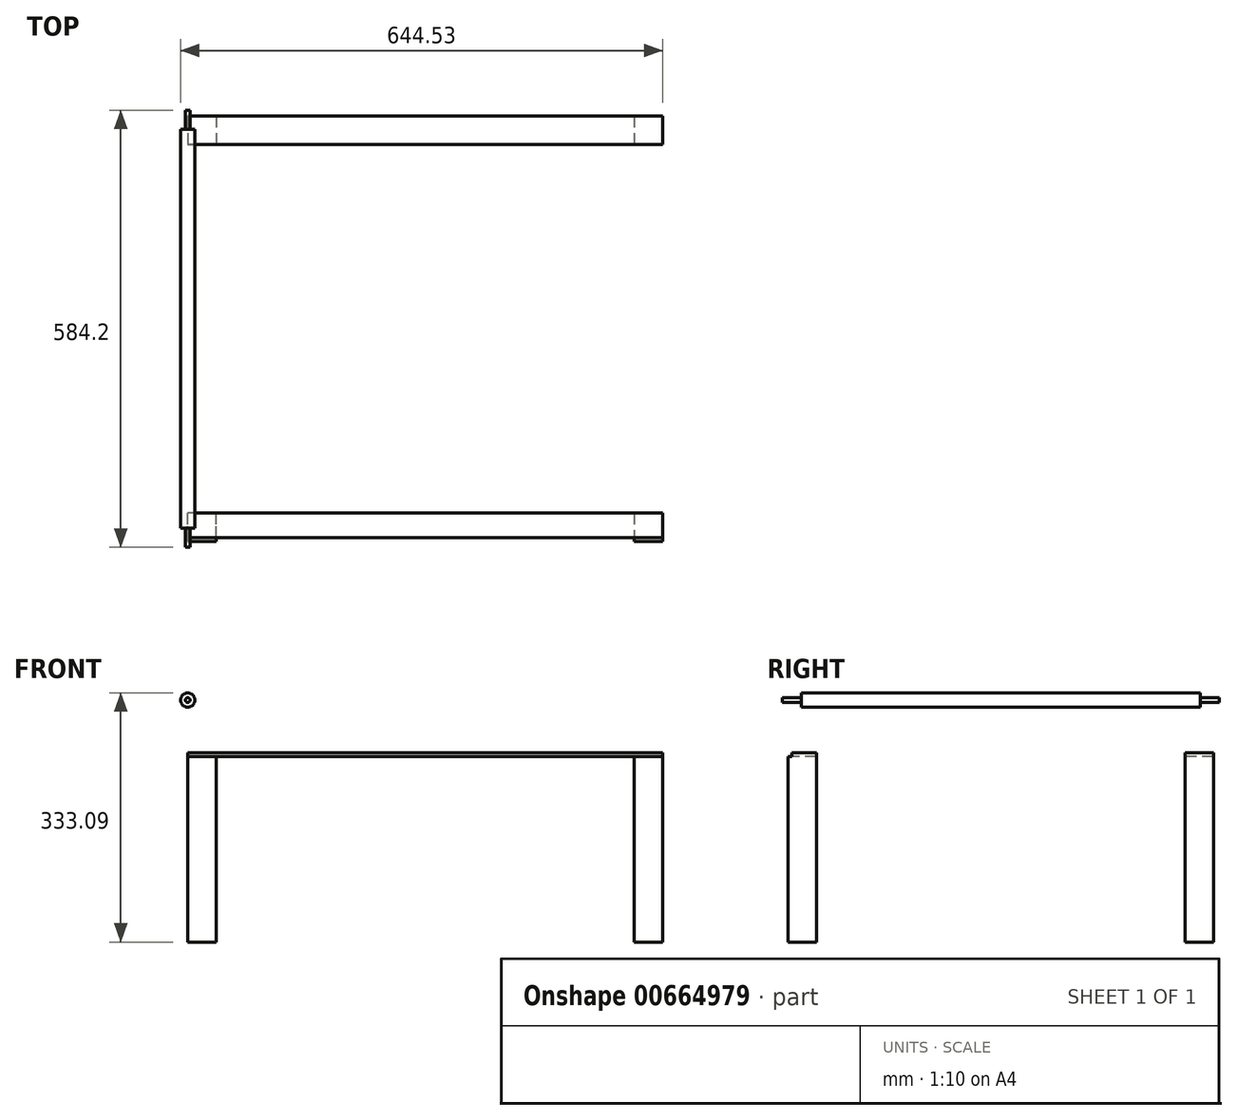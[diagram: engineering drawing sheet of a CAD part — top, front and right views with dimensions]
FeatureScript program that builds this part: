
annotation { "Feature Type Name" : "Feature", "Feature Type Description" : "" }
export const myFeature = defineFeature(function(context is Context, id is Id, definition is map)
    precondition{}
    {
        {
            var Q0;
            Q0=qCreatedBy(makeId("Front.planeOp"),FACE);
            var sketch = newSketch(context, id + "F0", { "sketchPlane" : qUnion([Q0])});
            skCircle(sketch, "E0", {"center": v(0, 0) * mm, "radius": 3.18 * mm});
            skSolve(sketch);
        }
        {
            var Q0;
            Q0=makeQuery(id+"F0.imprint","IMPRINT",FACE,{"disambiguationData":[TD([[makeQuery(id+"F0.imprint","IMPRINT",EDGE,{"derivedFrom":sQuery(id+"F0.wireOp",EDGE,"E0")}),1.0]])]});
            extrude(context, id + "F1", {"entities" : qUnion([Q0]), "endBound" : BoundingType.SYMMETRIC, "depth" : 584.2 * mm, "offsetDistance" : 25.4 * mm});
        }
        {
            var Q0;
            Q0=qCreatedBy(makeId("Front.planeOp"),FACE);
            var sketch = newSketch(context, id + "F2", { "sketchPlane" : qUnion([Q0])});
            skCircle(sketch, "E1", {"center": v(0, 0) * mm, "radius": 9.53 * mm});
            skSolve(sketch);
        }
        {
            var Q0;
            Q0=makeQuery(id+"F2.imprint","IMPRINT",FACE,{"disambiguationData":[TD([[makeQuery(id+"F2.imprint","IMPRINT",EDGE,{"derivedFrom":sQuery(id+"F2.wireOp",EDGE,"E1")}),1.0]])]});
            extrude(context, id + "F3", {"entities" : qUnion([Q0]), "operationType" : NewBodyOperationType.ADD, "endBound" : BoundingType.SYMMETRIC, "depth" : 533.4 * mm, "offsetDistance" : 25.4 * mm});
        }
        {
            var Q0;
            Q0=qCreatedBy(makeId("Right.planeOp"),FACE);
            var sketch = newSketch(context, id + "F4", { "sketchPlane" : qUnion([Q0])});
            skLineSegment(sketch, "E2.bottom", {"start": v(-284.48, -12.24) * mm, "end": v(-279.4, -12.24) * mm});
            skLineSegment(sketch, "E2.top", {"start": v(-284.48, -75.74) * mm, "end": v(-279.4, -75.74) * mm});
            skLineSegment(sketch, "E2.left", {"start": v(-284.48, -12.24) * mm, "end": v(-284.48, -75.74) * mm});
            skLineSegment(sketch, "E2.right", {"start": v(-279.4, -12.24) * mm, "end": v(-279.4, -75.74) * mm});
            skLineSegment(sketch, "E3.bottom", {"start": v(-284.48, -75.74) * mm, "end": v(-246.38, -75.74) * mm});
            skLineSegment(sketch, "E3.top", {"start": v(-284.48, -70.66) * mm, "end": v(-246.38, -70.66) * mm});
            skLineSegment(sketch, "E3.left", {"start": v(-284.48, -75.74) * mm, "end": v(-284.48, -70.66) * mm});
            skLineSegment(sketch, "E3.right", {"start": v(-246.38, -75.74) * mm, "end": v(-246.38, -70.66) * mm});
            skLineSegment(sketch, "E4", {"start": v(0, 0) * mm, "end": v(0, -41.11) * mm});
            skLineSegment(sketch, "E5.MirrorCS", {"start": v(284.48, -75.74) * mm, "end": v(284.48, -70.66) * mm});
            skLineSegment(sketch, "E6.MirrorCS", {"start": v(284.48, -12.24) * mm, "end": v(279.4, -12.24) * mm});
            skLineSegment(sketch, "E7.MirrorCS", {"start": v(246.38, -75.74) * mm, "end": v(246.38, -70.66) * mm});
            skLineSegment(sketch, "E8.MirrorCS", {"start": v(284.48, -75.74) * mm, "end": v(279.4, -75.74) * mm});
            skLineSegment(sketch, "E9.MirrorCS", {"start": v(284.48, -70.66) * mm, "end": v(246.38, -70.66) * mm});
            skLineSegment(sketch, "E10.MirrorCS", {"start": v(279.4, -12.24) * mm, "end": v(279.4, -75.74) * mm});
            skLineSegment(sketch, "E11.MirrorCS", {"start": v(284.48, -75.74) * mm, "end": v(246.38, -75.74) * mm});
            skLineSegment(sketch, "E12.MirrorCS", {"start": v(284.48, -12.24) * mm, "end": v(284.48, -75.74) * mm});
            skSolve(sketch);
        }
        {
            var Q0;
            {var subQ0=sQuery(id+"F4.wireOp",EDGE,"E2.bottom");Q0=makeQuery(id+"F4.imprint","IMPRINT",FACE,{"disambiguationData":[TD([[makeQuery(id+"F4.imprint","IMPRINT",EDGE,{"derivedFrom":subQ0}),-1.0]])]});}
            var Q1;
            {var subQ5=sQuery(id+"F4.wireOp",EDGE,"E3.left");Q1=makeQuery(id+"F4.imprint","IMPRINT",FACE,{"disambiguationData":[TD([[makeQuery(id+"F4.imprint","IMPRINT",EDGE,{"derivedFrom":subQ5}),-1.0]])]});}
            var Q2;
            {var subQ5=sQuery(id+"F4.wireOp",EDGE,"E3.right");Q2=makeQuery(id+"F4.imprint","IMPRINT",FACE,{"disambiguationData":[TD([[makeQuery(id+"F4.imprint","IMPRINT",EDGE,{"derivedFrom":subQ5}),1.0]])]});}
            var Q3;
            {var subQ0=sQuery(id+"F4.wireOp",EDGE,"E6.MirrorCS");Q3=makeQuery(id+"F4.imprint","IMPRINT",FACE,{"disambiguationData":[TD([[makeQuery(id+"F4.imprint","IMPRINT",EDGE,{"derivedFrom":subQ0}),1.0]])]});}
            var Q4;
            {var subQ0=sQuery(id+"F4.wireOp",EDGE,"E12.MirrorCS");var subQ1=sQuery(id+"F4.wireOp",EDGE,"E9.MirrorCS");var subQ2=makeQuery(id+"F4.imprint","INTERSECT",VERTEX,{"derivedFrom":[subQ1,subQ0]});Q4=makeQuery(id+"F4.imprint","IMPRINT",FACE,{"disambiguationData":[TD([[makeQuery(id+"F4.imprint","IMPRINT",EDGE,{"disambiguationData":[TD([[subQ2,-1.0]])],"derivedFrom":subQ1}),1.0]])]});}
            var Q5;
            {var subQ0=sQuery(id+"F4.wireOp",EDGE,"E7.MirrorCS");Q5=makeQuery(id+"F4.imprint","IMPRINT",FACE,{"disambiguationData":[TD([[makeQuery(id+"F4.imprint","IMPRINT",EDGE,{"derivedFrom":subQ0}),-1.0]])]});}
            extrude(context, id + "F5", {"entities" : qUnion([Q0, Q1, Q2, Q3, Q4, Q5]), "depth" : 635 * mm, "offsetDistance" : 25.4 * mm});
        }
        {
            var Q0;
            Q0=makeQuery(id+"F5.opExtrude","SWEPT_FACE",FACE,{"disambiguationData":[OSD([sQuery(id+"F4.wireOp",EDGE,"E2.left"),sQuery(id+"F4.wireOp",EDGE,"E3.left")])]});
            var sketch = newSketch(context, id + "F6", { "sketchPlane" : qUnion([Q0])});
            skLineSegment(sketch, "E13", {"start": v(0, -40.81) * mm, "end": v(635, -40.81) * mm});
            skCircle(sketch, "E14", {"center": v(9.53, -40.81) * mm, "radius": 3.18 * mm});
            skCircle(sketch, "E15.1.0.0", {"center": v(53.98, -40.81) * mm, "radius": 3.18 * mm});
            skCircle(sketch, "E15.2.0.0", {"center": v(98.43, -40.81) * mm, "radius": 3.18 * mm});
            skCircle(sketch, "E15.3.0.0", {"center": v(142.88, -40.81) * mm, "radius": 3.18 * mm});
            skCircle(sketch, "E15.4.0.0", {"center": v(187.33, -40.81) * mm, "radius": 3.18 * mm});
            skCircle(sketch, "E15.5.0.0", {"center": v(231.78, -40.81) * mm, "radius": 3.18 * mm});
            skCircle(sketch, "E15.6.0.0", {"center": v(276.23, -40.81) * mm, "radius": 3.18 * mm});
            skCircle(sketch, "E15.7.0.0", {"center": v(320.68, -40.81) * mm, "radius": 3.18 * mm});
            skLineSegment(sketch, "E15.direction1", {"start": v(9.53, -40.81) * mm, "end": v(53.98, -40.81) * mm, "construction": true});
            skLineSegment(sketch, "E16", {"start": v(0, -18.59) * mm, "end": v(393.7, -18.59) * mm});
            skCircle(sketch, "E17", {"center": v(9.53, -18.59) * mm, "radius": 3.18 * mm});
            skCircle(sketch, "E18.1.0.0", {"center": v(53.98, -18.59) * mm, "radius": 3.18 * mm});
            skCircle(sketch, "E18.2.0.0", {"center": v(98.43, -18.59) * mm, "radius": 3.18 * mm});
            skCircle(sketch, "E18.3.0.0", {"center": v(142.88, -18.59) * mm, "radius": 3.18 * mm});
            skCircle(sketch, "E18.4.0.0", {"center": v(187.33, -18.59) * mm, "radius": 3.18 * mm});
            skCircle(sketch, "E18.5.0.0", {"center": v(231.78, -18.59) * mm, "radius": 3.18 * mm});
            skCircle(sketch, "E18.6.0.0", {"center": v(276.23, -18.59) * mm, "radius": 3.18 * mm});
            skCircle(sketch, "E18.7.0.0", {"center": v(320.68, -18.59) * mm, "radius": 3.18 * mm});
            skLineSegment(sketch, "E18.direction1", {"start": v(9.53, -18.59) * mm, "end": v(53.98, -18.59) * mm, "construction": true});
            skCircle(sketch, "E19.0.8.0", {"center": v(365.13, -18.59) * mm, "radius": 3.18 * mm});
            skCircle(sketch, "E20.0.8.0", {"center": v(365.13, -40.81) * mm, "radius": 3.18 * mm});
            skCircle(sketch, "E21.0.9.0", {"center": v(409.58, -40.81) * mm, "radius": 3.18 * mm});
            skCircle(sketch, "E21.0.10.0", {"center": v(454.03, -40.81) * mm, "radius": 3.18 * mm});
            skCircle(sketch, "E21.0.11.0", {"center": v(498.48, -40.81) * mm, "radius": 3.18 * mm});
            skCircle(sketch, "E21.0.12.0", {"center": v(542.93, -40.81) * mm, "radius": 3.18 * mm});
            skCircle(sketch, "E21.0.13.0", {"center": v(587.38, -40.81) * mm, "radius": 3.18 * mm});
            skCircle(sketch, "E22.0.9.0", {"center": v(409.58, -18.59) * mm, "radius": 3.18 * mm});
            skCircle(sketch, "E22.0.10.0", {"center": v(454.03, -18.59) * mm, "radius": 3.18 * mm});
            skCircle(sketch, "E22.0.11.0", {"center": v(498.48, -18.59) * mm, "radius": 3.18 * mm});
            skCircle(sketch, "E22.0.12.0", {"center": v(542.93, -18.59) * mm, "radius": 3.18 * mm});
            skCircle(sketch, "E22.0.13.0", {"center": v(587.38, -18.59) * mm, "radius": 3.18 * mm});
            skLineSegment(sketch, "E23", {"start": v(393.7, -18.59) * mm, "end": v(635, -18.59) * mm});
            skSolve(sketch);
        }
        {
            var Q0;
            {var subQ0=sQuery(id+"F6.wireOp",EDGE,"E14");var subQ1=sQuery(id+"F6.wireOp",EDGE,"E13");var subQ2=makeQuery(id+"F6.imprint","INTERSECT",VERTEX,{"disambiguationData":[OD(0.0)],"derivedFrom":[subQ1,subQ0]});Q0=makeQuery(id+"F6.imprint","IMPRINT",FACE,{"disambiguationData":[TD([[makeQuery(id+"F6.imprint","IMPRINT",EDGE,{"disambiguationData":[TD([[subQ2,-1.0]])],"derivedFrom":subQ1}),1.0]])]});}
            var Q1;
            {var subQ0=sQuery(id+"F6.wireOp",EDGE,"E14");var subQ1=sQuery(id+"F6.wireOp",EDGE,"E13");var subQ2=makeQuery(id+"F6.imprint","INTERSECT",VERTEX,{"disambiguationData":[OD(0.0)],"derivedFrom":[subQ1,subQ0]});Q1=makeQuery(id+"F6.imprint","IMPRINT",FACE,{"disambiguationData":[TD([[makeQuery(id+"F6.imprint","IMPRINT",EDGE,{"disambiguationData":[TD([[subQ2,-1.0]])],"derivedFrom":subQ1}),-1.0]])]});}
            var Q2;
            {var subQ0=sQuery(id+"F6.wireOp",EDGE,"E15.1.0.0");var subQ1=sQuery(id+"F6.wireOp",EDGE,"E13");var subQ2=makeQuery(id+"F6.imprint","INTERSECT",VERTEX,{"disambiguationData":[OD(0.0)],"derivedFrom":[subQ1,subQ0]});Q2=makeQuery(id+"F6.imprint","IMPRINT",FACE,{"disambiguationData":[TD([[makeQuery(id+"F6.imprint","IMPRINT",EDGE,{"disambiguationData":[TD([[subQ2,-1.0]])],"derivedFrom":subQ1}),1.0]])]});}
            var Q3;
            {var subQ0=sQuery(id+"F6.wireOp",EDGE,"E15.2.0.0");var subQ1=sQuery(id+"F6.wireOp",EDGE,"E13");var subQ2=makeQuery(id+"F6.imprint","INTERSECT",VERTEX,{"disambiguationData":[OD(0.0)],"derivedFrom":[subQ1,subQ0]});Q3=makeQuery(id+"F6.imprint","IMPRINT",FACE,{"disambiguationData":[TD([[makeQuery(id+"F6.imprint","IMPRINT",EDGE,{"disambiguationData":[TD([[subQ2,-1.0]])],"derivedFrom":subQ1}),1.0]])]});}
            var Q4;
            {var subQ0=sQuery(id+"F6.wireOp",EDGE,"E15.2.0.0");var subQ1=sQuery(id+"F6.wireOp",EDGE,"E13");var subQ2=makeQuery(id+"F6.imprint","INTERSECT",VERTEX,{"disambiguationData":[OD(0.0)],"derivedFrom":[subQ1,subQ0]});Q4=makeQuery(id+"F6.imprint","IMPRINT",FACE,{"disambiguationData":[TD([[makeQuery(id+"F6.imprint","IMPRINT",EDGE,{"disambiguationData":[TD([[subQ2,-1.0]])],"derivedFrom":subQ1}),-1.0]])]});}
            var Q5;
            {var subQ0=sQuery(id+"F6.wireOp",EDGE,"E15.1.0.0");var subQ1=sQuery(id+"F6.wireOp",EDGE,"E13");var subQ2=makeQuery(id+"F6.imprint","INTERSECT",VERTEX,{"disambiguationData":[OD(0.0)],"derivedFrom":[subQ1,subQ0]});Q5=makeQuery(id+"F6.imprint","IMPRINT",FACE,{"disambiguationData":[TD([[makeQuery(id+"F6.imprint","IMPRINT",EDGE,{"disambiguationData":[TD([[subQ2,-1.0]])],"derivedFrom":subQ1}),-1.0]])]});}
            var Q6;
            {var subQ0=sQuery(id+"F6.wireOp",EDGE,"E15.3.0.0");var subQ1=sQuery(id+"F6.wireOp",EDGE,"E13");var subQ2=makeQuery(id+"F6.imprint","INTERSECT",VERTEX,{"disambiguationData":[OD(0.0)],"derivedFrom":[subQ1,subQ0]});Q6=makeQuery(id+"F6.imprint","IMPRINT",FACE,{"disambiguationData":[TD([[makeQuery(id+"F6.imprint","IMPRINT",EDGE,{"disambiguationData":[TD([[subQ2,-1.0]])],"derivedFrom":subQ1}),-1.0]])]});}
            var Q7;
            {var subQ0=sQuery(id+"F6.wireOp",EDGE,"E15.3.0.0");var subQ1=sQuery(id+"F6.wireOp",EDGE,"E13");var subQ2=makeQuery(id+"F6.imprint","INTERSECT",VERTEX,{"disambiguationData":[OD(0.0)],"derivedFrom":[subQ1,subQ0]});Q7=makeQuery(id+"F6.imprint","IMPRINT",FACE,{"disambiguationData":[TD([[makeQuery(id+"F6.imprint","IMPRINT",EDGE,{"disambiguationData":[TD([[subQ2,-1.0]])],"derivedFrom":subQ1}),1.0]])]});}
            var Q8;
            {var subQ0=sQuery(id+"F6.wireOp",EDGE,"E15.4.0.0");var subQ1=sQuery(id+"F6.wireOp",EDGE,"E13");var subQ2=makeQuery(id+"F6.imprint","INTERSECT",VERTEX,{"disambiguationData":[OD(0.0)],"derivedFrom":[subQ1,subQ0]});Q8=makeQuery(id+"F6.imprint","IMPRINT",FACE,{"disambiguationData":[TD([[makeQuery(id+"F6.imprint","IMPRINT",EDGE,{"disambiguationData":[TD([[subQ2,-1.0]])],"derivedFrom":subQ1}),1.0]])]});}
            var Q9;
            {var subQ0=sQuery(id+"F6.wireOp",EDGE,"E15.4.0.0");var subQ1=sQuery(id+"F6.wireOp",EDGE,"E13");var subQ2=makeQuery(id+"F6.imprint","INTERSECT",VERTEX,{"disambiguationData":[OD(0.0)],"derivedFrom":[subQ1,subQ0]});Q9=makeQuery(id+"F6.imprint","IMPRINT",FACE,{"disambiguationData":[TD([[makeQuery(id+"F6.imprint","IMPRINT",EDGE,{"disambiguationData":[TD([[subQ2,-1.0]])],"derivedFrom":subQ1}),-1.0]])]});}
            var Q10;
            {var subQ0=sQuery(id+"F6.wireOp",EDGE,"E15.5.0.0");var subQ1=sQuery(id+"F6.wireOp",EDGE,"E13");var subQ2=makeQuery(id+"F6.imprint","INTERSECT",VERTEX,{"disambiguationData":[OD(0.0)],"derivedFrom":[subQ1,subQ0]});Q10=makeQuery(id+"F6.imprint","IMPRINT",FACE,{"disambiguationData":[TD([[makeQuery(id+"F6.imprint","IMPRINT",EDGE,{"disambiguationData":[TD([[subQ2,-1.0]])],"derivedFrom":subQ1}),1.0]])]});}
            var Q11;
            {var subQ0=sQuery(id+"F6.wireOp",EDGE,"E15.5.0.0");var subQ1=sQuery(id+"F6.wireOp",EDGE,"E13");var subQ2=makeQuery(id+"F6.imprint","INTERSECT",VERTEX,{"disambiguationData":[OD(0.0)],"derivedFrom":[subQ1,subQ0]});Q11=makeQuery(id+"F6.imprint","IMPRINT",FACE,{"disambiguationData":[TD([[makeQuery(id+"F6.imprint","IMPRINT",EDGE,{"disambiguationData":[TD([[subQ2,-1.0]])],"derivedFrom":subQ1}),-1.0]])]});}
            var Q12;
            {var subQ0=sQuery(id+"F6.wireOp",EDGE,"E15.6.0.0");var subQ1=sQuery(id+"F6.wireOp",EDGE,"E13");var subQ2=makeQuery(id+"F6.imprint","INTERSECT",VERTEX,{"disambiguationData":[OD(0.0)],"derivedFrom":[subQ1,subQ0]});Q12=makeQuery(id+"F6.imprint","IMPRINT",FACE,{"disambiguationData":[TD([[makeQuery(id+"F6.imprint","IMPRINT",EDGE,{"disambiguationData":[TD([[subQ2,-1.0]])],"derivedFrom":subQ1}),-1.0]])]});}
            var Q13;
            {var subQ0=sQuery(id+"F6.wireOp",EDGE,"E15.6.0.0");var subQ1=sQuery(id+"F6.wireOp",EDGE,"E13");var subQ2=makeQuery(id+"F6.imprint","INTERSECT",VERTEX,{"disambiguationData":[OD(0.0)],"derivedFrom":[subQ1,subQ0]});Q13=makeQuery(id+"F6.imprint","IMPRINT",FACE,{"disambiguationData":[TD([[makeQuery(id+"F6.imprint","IMPRINT",EDGE,{"disambiguationData":[TD([[subQ2,-1.0]])],"derivedFrom":subQ1}),1.0]])]});}
            var Q14;
            {var subQ0=sQuery(id+"F6.wireOp",EDGE,"E15.7.0.0");var subQ1=sQuery(id+"F6.wireOp",EDGE,"E13");var subQ2=makeQuery(id+"F6.imprint","INTERSECT",VERTEX,{"disambiguationData":[OD(0.0)],"derivedFrom":[subQ1,subQ0]});Q14=makeQuery(id+"F6.imprint","IMPRINT",FACE,{"disambiguationData":[TD([[makeQuery(id+"F6.imprint","IMPRINT",EDGE,{"disambiguationData":[TD([[subQ2,-1.0]])],"derivedFrom":subQ1}),-1.0]])]});}
            var Q15;
            {var subQ0=sQuery(id+"F6.wireOp",EDGE,"E15.7.0.0");var subQ1=sQuery(id+"F6.wireOp",EDGE,"E13");var subQ2=makeQuery(id+"F6.imprint","INTERSECT",VERTEX,{"disambiguationData":[OD(0.0)],"derivedFrom":[subQ1,subQ0]});Q15=makeQuery(id+"F6.imprint","IMPRINT",FACE,{"disambiguationData":[TD([[makeQuery(id+"F6.imprint","IMPRINT",EDGE,{"disambiguationData":[TD([[subQ2,-1.0]])],"derivedFrom":subQ1}),1.0]])]});}
            var Q16;
            {var subQ0=sQuery(id+"F6.wireOp",EDGE,"E17");var subQ1=sQuery(id+"F6.wireOp",EDGE,"E16");var subQ2=makeQuery(id+"F6.imprint","INTERSECT",VERTEX,{"disambiguationData":[OD(0.0)],"derivedFrom":[subQ1,subQ0]});Q16=makeQuery(id+"F6.imprint","IMPRINT",FACE,{"disambiguationData":[TD([[makeQuery(id+"F6.imprint","IMPRINT",EDGE,{"disambiguationData":[TD([[subQ2,-1.0]])],"derivedFrom":subQ1}),1.0]])]});}
            var Q17;
            {var subQ0=sQuery(id+"F6.wireOp",EDGE,"E17");var subQ1=sQuery(id+"F6.wireOp",EDGE,"E16");var subQ2=makeQuery(id+"F6.imprint","INTERSECT",VERTEX,{"disambiguationData":[OD(0.0)],"derivedFrom":[subQ1,subQ0]});Q17=makeQuery(id+"F6.imprint","IMPRINT",FACE,{"disambiguationData":[TD([[makeQuery(id+"F6.imprint","IMPRINT",EDGE,{"disambiguationData":[TD([[subQ2,-1.0]])],"derivedFrom":subQ1}),-1.0]])]});}
            var Q18;
            {var subQ0=sQuery(id+"F6.wireOp",EDGE,"E18.1.0.0");var subQ1=sQuery(id+"F6.wireOp",EDGE,"E16");var subQ2=makeQuery(id+"F6.imprint","INTERSECT",VERTEX,{"disambiguationData":[OD(0.0)],"derivedFrom":[subQ1,subQ0]});Q18=makeQuery(id+"F6.imprint","IMPRINT",FACE,{"disambiguationData":[TD([[makeQuery(id+"F6.imprint","IMPRINT",EDGE,{"disambiguationData":[TD([[subQ2,-1.0]])],"derivedFrom":subQ1}),1.0]])]});}
            var Q19;
            {var subQ0=sQuery(id+"F6.wireOp",EDGE,"E18.1.0.0");var subQ1=sQuery(id+"F6.wireOp",EDGE,"E16");var subQ2=makeQuery(id+"F6.imprint","INTERSECT",VERTEX,{"disambiguationData":[OD(0.0)],"derivedFrom":[subQ1,subQ0]});Q19=makeQuery(id+"F6.imprint","IMPRINT",FACE,{"disambiguationData":[TD([[makeQuery(id+"F6.imprint","IMPRINT",EDGE,{"disambiguationData":[TD([[subQ2,-1.0]])],"derivedFrom":subQ1}),-1.0]])]});}
            var Q20;
            {var subQ0=sQuery(id+"F6.wireOp",EDGE,"E18.2.0.0");var subQ1=sQuery(id+"F6.wireOp",EDGE,"E16");var subQ2=makeQuery(id+"F6.imprint","INTERSECT",VERTEX,{"disambiguationData":[OD(0.0)],"derivedFrom":[subQ1,subQ0]});Q20=makeQuery(id+"F6.imprint","IMPRINT",FACE,{"disambiguationData":[TD([[makeQuery(id+"F6.imprint","IMPRINT",EDGE,{"disambiguationData":[TD([[subQ2,-1.0]])],"derivedFrom":subQ1}),-1.0]])]});}
            var Q21;
            {var subQ0=sQuery(id+"F6.wireOp",EDGE,"E18.2.0.0");var subQ1=sQuery(id+"F6.wireOp",EDGE,"E16");var subQ2=makeQuery(id+"F6.imprint","INTERSECT",VERTEX,{"disambiguationData":[OD(0.0)],"derivedFrom":[subQ1,subQ0]});Q21=makeQuery(id+"F6.imprint","IMPRINT",FACE,{"disambiguationData":[TD([[makeQuery(id+"F6.imprint","IMPRINT",EDGE,{"disambiguationData":[TD([[subQ2,-1.0]])],"derivedFrom":subQ1}),1.0]])]});}
            var Q22;
            {var subQ0=sQuery(id+"F6.wireOp",EDGE,"E18.3.0.0");var subQ1=sQuery(id+"F6.wireOp",EDGE,"E16");var subQ2=makeQuery(id+"F6.imprint","INTERSECT",VERTEX,{"disambiguationData":[OD(0.0)],"derivedFrom":[subQ1,subQ0]});Q22=makeQuery(id+"F6.imprint","IMPRINT",FACE,{"disambiguationData":[TD([[makeQuery(id+"F6.imprint","IMPRINT",EDGE,{"disambiguationData":[TD([[subQ2,-1.0]])],"derivedFrom":subQ1}),-1.0]])]});}
            var Q23;
            {var subQ0=sQuery(id+"F6.wireOp",EDGE,"E18.3.0.0");var subQ1=sQuery(id+"F6.wireOp",EDGE,"E16");var subQ2=makeQuery(id+"F6.imprint","INTERSECT",VERTEX,{"disambiguationData":[OD(0.0)],"derivedFrom":[subQ1,subQ0]});Q23=makeQuery(id+"F6.imprint","IMPRINT",FACE,{"disambiguationData":[TD([[makeQuery(id+"F6.imprint","IMPRINT",EDGE,{"disambiguationData":[TD([[subQ2,-1.0]])],"derivedFrom":subQ1}),1.0]])]});}
            var Q24;
            {var subQ0=sQuery(id+"F6.wireOp",EDGE,"E18.4.0.0");var subQ1=sQuery(id+"F6.wireOp",EDGE,"E16");var subQ2=makeQuery(id+"F6.imprint","INTERSECT",VERTEX,{"disambiguationData":[OD(0.0)],"derivedFrom":[subQ1,subQ0]});Q24=makeQuery(id+"F6.imprint","IMPRINT",FACE,{"disambiguationData":[TD([[makeQuery(id+"F6.imprint","IMPRINT",EDGE,{"disambiguationData":[TD([[subQ2,-1.0]])],"derivedFrom":subQ1}),-1.0]])]});}
            var Q25;
            {var subQ0=sQuery(id+"F6.wireOp",EDGE,"E18.4.0.0");var subQ1=sQuery(id+"F6.wireOp",EDGE,"E16");var subQ2=makeQuery(id+"F6.imprint","INTERSECT",VERTEX,{"disambiguationData":[OD(0.0)],"derivedFrom":[subQ1,subQ0]});Q25=makeQuery(id+"F6.imprint","IMPRINT",FACE,{"disambiguationData":[TD([[makeQuery(id+"F6.imprint","IMPRINT",EDGE,{"disambiguationData":[TD([[subQ2,-1.0]])],"derivedFrom":subQ1}),1.0]])]});}
            var Q26;
            {var subQ0=sQuery(id+"F6.wireOp",EDGE,"E18.5.0.0");var subQ1=sQuery(id+"F6.wireOp",EDGE,"E16");var subQ2=makeQuery(id+"F6.imprint","INTERSECT",VERTEX,{"disambiguationData":[OD(0.0)],"derivedFrom":[subQ1,subQ0]});Q26=makeQuery(id+"F6.imprint","IMPRINT",FACE,{"disambiguationData":[TD([[makeQuery(id+"F6.imprint","IMPRINT",EDGE,{"disambiguationData":[TD([[subQ2,-1.0]])],"derivedFrom":subQ1}),-1.0]])]});}
            var Q27;
            {var subQ0=sQuery(id+"F6.wireOp",EDGE,"E18.5.0.0");var subQ1=sQuery(id+"F6.wireOp",EDGE,"E16");var subQ2=makeQuery(id+"F6.imprint","INTERSECT",VERTEX,{"disambiguationData":[OD(0.0)],"derivedFrom":[subQ1,subQ0]});Q27=makeQuery(id+"F6.imprint","IMPRINT",FACE,{"disambiguationData":[TD([[makeQuery(id+"F6.imprint","IMPRINT",EDGE,{"disambiguationData":[TD([[subQ2,-1.0]])],"derivedFrom":subQ1}),1.0]])]});}
            var Q28;
            {var subQ0=sQuery(id+"F6.wireOp",EDGE,"E18.6.0.0");var subQ1=sQuery(id+"F6.wireOp",EDGE,"E16");var subQ2=makeQuery(id+"F6.imprint","INTERSECT",VERTEX,{"disambiguationData":[OD(0.0)],"derivedFrom":[subQ1,subQ0]});Q28=makeQuery(id+"F6.imprint","IMPRINT",FACE,{"disambiguationData":[TD([[makeQuery(id+"F6.imprint","IMPRINT",EDGE,{"disambiguationData":[TD([[subQ2,-1.0]])],"derivedFrom":subQ1}),-1.0]])]});}
            var Q29;
            {var subQ0=sQuery(id+"F6.wireOp",EDGE,"E18.6.0.0");var subQ1=sQuery(id+"F6.wireOp",EDGE,"E16");var subQ2=makeQuery(id+"F6.imprint","INTERSECT",VERTEX,{"disambiguationData":[OD(0.0)],"derivedFrom":[subQ1,subQ0]});Q29=makeQuery(id+"F6.imprint","IMPRINT",FACE,{"disambiguationData":[TD([[makeQuery(id+"F6.imprint","IMPRINT",EDGE,{"disambiguationData":[TD([[subQ2,-1.0]])],"derivedFrom":subQ1}),1.0]])]});}
            var Q30;
            {var subQ0=sQuery(id+"F6.wireOp",EDGE,"E18.7.0.0");var subQ1=sQuery(id+"F6.wireOp",EDGE,"E16");var subQ2=makeQuery(id+"F6.imprint","INTERSECT",VERTEX,{"disambiguationData":[OD(0.0)],"derivedFrom":[subQ1,subQ0]});Q30=makeQuery(id+"F6.imprint","IMPRINT",FACE,{"disambiguationData":[TD([[makeQuery(id+"F6.imprint","IMPRINT",EDGE,{"disambiguationData":[TD([[subQ2,-1.0]])],"derivedFrom":subQ1}),-1.0]])]});}
            var Q31;
            {var subQ0=sQuery(id+"F6.wireOp",EDGE,"E18.7.0.0");var subQ1=sQuery(id+"F6.wireOp",EDGE,"E16");var subQ2=makeQuery(id+"F6.imprint","INTERSECT",VERTEX,{"disambiguationData":[OD(0.0)],"derivedFrom":[subQ1,subQ0]});Q31=makeQuery(id+"F6.imprint","IMPRINT",FACE,{"disambiguationData":[TD([[makeQuery(id+"F6.imprint","IMPRINT",EDGE,{"disambiguationData":[TD([[subQ2,-1.0]])],"derivedFrom":subQ1}),1.0]])]});}
            var Q32;
            {var subQ0=sQuery(id+"F6.wireOp",EDGE,"E20.0.8.0");var subQ1=sQuery(id+"F6.wireOp",EDGE,"E13");var subQ2=makeQuery(id+"F6.imprint","INTERSECT",VERTEX,{"disambiguationData":[OD(0.0)],"derivedFrom":[subQ1,subQ0]});Q32=makeQuery(id+"F6.imprint","IMPRINT",FACE,{"disambiguationData":[TD([[makeQuery(id+"F6.imprint","IMPRINT",EDGE,{"disambiguationData":[TD([[subQ2,-1.0]])],"derivedFrom":subQ1}),-1.0]])]});}
            var Q33;
            {var subQ0=sQuery(id+"F6.wireOp",EDGE,"E20.0.8.0");var subQ1=sQuery(id+"F6.wireOp",EDGE,"E13");var subQ2=makeQuery(id+"F6.imprint","INTERSECT",VERTEX,{"disambiguationData":[OD(0.0)],"derivedFrom":[subQ1,subQ0]});Q33=makeQuery(id+"F6.imprint","IMPRINT",FACE,{"disambiguationData":[TD([[makeQuery(id+"F6.imprint","IMPRINT",EDGE,{"disambiguationData":[TD([[subQ2,-1.0]])],"derivedFrom":subQ1}),1.0]])]});}
            var Q34;
            {var subQ0=sQuery(id+"F6.wireOp",EDGE,"E19.0.8.0");var subQ1=sQuery(id+"F6.wireOp",EDGE,"E16");var subQ2=makeQuery(id+"F6.imprint","INTERSECT",VERTEX,{"disambiguationData":[OD(0.0)],"derivedFrom":[subQ1,subQ0]});Q34=makeQuery(id+"F6.imprint","IMPRINT",FACE,{"disambiguationData":[TD([[makeQuery(id+"F6.imprint","IMPRINT",EDGE,{"disambiguationData":[TD([[subQ2,-1.0]])],"derivedFrom":subQ1}),1.0]])]});}
            var Q35;
            {var subQ0=sQuery(id+"F6.wireOp",EDGE,"E19.0.8.0");var subQ1=sQuery(id+"F6.wireOp",EDGE,"E16");var subQ2=makeQuery(id+"F6.imprint","INTERSECT",VERTEX,{"disambiguationData":[OD(0.0)],"derivedFrom":[subQ1,subQ0]});Q35=makeQuery(id+"F6.imprint","IMPRINT",FACE,{"disambiguationData":[TD([[makeQuery(id+"F6.imprint","IMPRINT",EDGE,{"disambiguationData":[TD([[subQ2,-1.0]])],"derivedFrom":subQ1}),-1.0]])]});}
            var Q36;
            {var subQ0=sQuery(id+"F6.wireOp",EDGE,"E23");var subQ1=sQuery(id+"F6.wireOp",EDGE,"E22.0.9.0");var subQ2=makeQuery(id+"F6.imprint","INTERSECT",VERTEX,{"disambiguationData":[OD(0.0)],"derivedFrom":[subQ1,subQ0]});Q36=makeQuery(id+"F6.imprint","IMPRINT",FACE,{"disambiguationData":[TD([[makeQuery(id+"F6.imprint","IMPRINT",EDGE,{"disambiguationData":[TD([[subQ2,-1.0]])],"derivedFrom":subQ1}),1.0]])]});}
            var Q37;
            {var subQ0=sQuery(id+"F6.wireOp",EDGE,"E23");var subQ1=sQuery(id+"F6.wireOp",EDGE,"E22.0.9.0");var subQ2=makeQuery(id+"F6.imprint","INTERSECT",VERTEX,{"disambiguationData":[OD(0.0)],"derivedFrom":[subQ1,subQ0]});Q37=makeQuery(id+"F6.imprint","IMPRINT",FACE,{"disambiguationData":[TD([[makeQuery(id+"F6.imprint","IMPRINT",EDGE,{"disambiguationData":[TD([[subQ2,1.0]])],"derivedFrom":subQ1}),1.0]])]});}
            var Q38;
            {var subQ0=sQuery(id+"F6.wireOp",EDGE,"E23");var subQ1=sQuery(id+"F6.wireOp",EDGE,"E22.0.10.0");var subQ2=makeQuery(id+"F6.imprint","INTERSECT",VERTEX,{"disambiguationData":[OD(0.0)],"derivedFrom":[subQ1,subQ0]});Q38=makeQuery(id+"F6.imprint","IMPRINT",FACE,{"disambiguationData":[TD([[makeQuery(id+"F6.imprint","IMPRINT",EDGE,{"disambiguationData":[TD([[subQ2,1.0]])],"derivedFrom":subQ1}),1.0]])]});}
            var Q39;
            {var subQ0=sQuery(id+"F6.wireOp",EDGE,"E23");var subQ1=sQuery(id+"F6.wireOp",EDGE,"E22.0.10.0");var subQ2=makeQuery(id+"F6.imprint","INTERSECT",VERTEX,{"disambiguationData":[OD(0.0)],"derivedFrom":[subQ1,subQ0]});Q39=makeQuery(id+"F6.imprint","IMPRINT",FACE,{"disambiguationData":[TD([[makeQuery(id+"F6.imprint","IMPRINT",EDGE,{"disambiguationData":[TD([[subQ2,-1.0]])],"derivedFrom":subQ1}),1.0]])]});}
            var Q40;
            {var subQ0=sQuery(id+"F6.wireOp",EDGE,"E23");var subQ1=sQuery(id+"F6.wireOp",EDGE,"E22.0.11.0");var subQ2=makeQuery(id+"F6.imprint","INTERSECT",VERTEX,{"disambiguationData":[OD(0.0)],"derivedFrom":[subQ1,subQ0]});Q40=makeQuery(id+"F6.imprint","IMPRINT",FACE,{"disambiguationData":[TD([[makeQuery(id+"F6.imprint","IMPRINT",EDGE,{"disambiguationData":[TD([[subQ2,1.0]])],"derivedFrom":subQ1}),1.0]])]});}
            var Q41;
            {var subQ0=sQuery(id+"F6.wireOp",EDGE,"E23");var subQ1=sQuery(id+"F6.wireOp",EDGE,"E22.0.11.0");var subQ2=makeQuery(id+"F6.imprint","INTERSECT",VERTEX,{"disambiguationData":[OD(0.0)],"derivedFrom":[subQ1,subQ0]});Q41=makeQuery(id+"F6.imprint","IMPRINT",FACE,{"disambiguationData":[TD([[makeQuery(id+"F6.imprint","IMPRINT",EDGE,{"disambiguationData":[TD([[subQ2,-1.0]])],"derivedFrom":subQ1}),1.0]])]});}
            var Q42;
            {var subQ0=sQuery(id+"F6.wireOp",EDGE,"E23");var subQ1=sQuery(id+"F6.wireOp",EDGE,"E22.0.12.0");var subQ2=makeQuery(id+"F6.imprint","INTERSECT",VERTEX,{"disambiguationData":[OD(0.0)],"derivedFrom":[subQ1,subQ0]});Q42=makeQuery(id+"F6.imprint","IMPRINT",FACE,{"disambiguationData":[TD([[makeQuery(id+"F6.imprint","IMPRINT",EDGE,{"disambiguationData":[TD([[subQ2,1.0]])],"derivedFrom":subQ1}),1.0]])]});}
            var Q43;
            {var subQ0=sQuery(id+"F6.wireOp",EDGE,"E23");var subQ1=sQuery(id+"F6.wireOp",EDGE,"E22.0.12.0");var subQ2=makeQuery(id+"F6.imprint","INTERSECT",VERTEX,{"disambiguationData":[OD(0.0)],"derivedFrom":[subQ1,subQ0]});Q43=makeQuery(id+"F6.imprint","IMPRINT",FACE,{"disambiguationData":[TD([[makeQuery(id+"F6.imprint","IMPRINT",EDGE,{"disambiguationData":[TD([[subQ2,-1.0]])],"derivedFrom":subQ1}),1.0]])]});}
            var Q44;
            {var subQ0=sQuery(id+"F6.wireOp",EDGE,"E23");var subQ1=sQuery(id+"F6.wireOp",EDGE,"E22.0.13.0");var subQ2=makeQuery(id+"F6.imprint","INTERSECT",VERTEX,{"disambiguationData":[OD(0.0)],"derivedFrom":[subQ1,subQ0]});Q44=makeQuery(id+"F6.imprint","IMPRINT",FACE,{"disambiguationData":[TD([[makeQuery(id+"F6.imprint","IMPRINT",EDGE,{"disambiguationData":[TD([[subQ2,1.0]])],"derivedFrom":subQ1}),1.0]])]});}
            var Q45;
            {var subQ0=sQuery(id+"F6.wireOp",EDGE,"E23");var subQ1=sQuery(id+"F6.wireOp",EDGE,"E22.0.13.0");var subQ2=makeQuery(id+"F6.imprint","INTERSECT",VERTEX,{"disambiguationData":[OD(0.0)],"derivedFrom":[subQ1,subQ0]});Q45=makeQuery(id+"F6.imprint","IMPRINT",FACE,{"disambiguationData":[TD([[makeQuery(id+"F6.imprint","IMPRINT",EDGE,{"disambiguationData":[TD([[subQ2,-1.0]])],"derivedFrom":subQ1}),1.0]])]});}
            var Q46;
            {var subQ0=sQuery(id+"F6.wireOp",EDGE,"E21.0.9.0");var subQ1=sQuery(id+"F6.wireOp",EDGE,"E13");var subQ2=makeQuery(id+"F6.imprint","INTERSECT",VERTEX,{"disambiguationData":[OD(0.0)],"derivedFrom":[subQ1,subQ0]});Q46=makeQuery(id+"F6.imprint","IMPRINT",FACE,{"disambiguationData":[TD([[makeQuery(id+"F6.imprint","IMPRINT",EDGE,{"disambiguationData":[TD([[subQ2,-1.0]])],"derivedFrom":subQ1}),1.0]])]});}
            var Q47;
            {var subQ0=sQuery(id+"F6.wireOp",EDGE,"E21.0.9.0");var subQ1=sQuery(id+"F6.wireOp",EDGE,"E13");var subQ2=makeQuery(id+"F6.imprint","INTERSECT",VERTEX,{"disambiguationData":[OD(0.0)],"derivedFrom":[subQ1,subQ0]});Q47=makeQuery(id+"F6.imprint","IMPRINT",FACE,{"disambiguationData":[TD([[makeQuery(id+"F6.imprint","IMPRINT",EDGE,{"disambiguationData":[TD([[subQ2,-1.0]])],"derivedFrom":subQ1}),-1.0]])]});}
            var Q48;
            {var subQ0=sQuery(id+"F6.wireOp",EDGE,"E21.0.10.0");var subQ1=sQuery(id+"F6.wireOp",EDGE,"E13");var subQ2=makeQuery(id+"F6.imprint","INTERSECT",VERTEX,{"disambiguationData":[OD(0.0)],"derivedFrom":[subQ1,subQ0]});Q48=makeQuery(id+"F6.imprint","IMPRINT",FACE,{"disambiguationData":[TD([[makeQuery(id+"F6.imprint","IMPRINT",EDGE,{"disambiguationData":[TD([[subQ2,-1.0]])],"derivedFrom":subQ1}),1.0]])]});}
            var Q49;
            {var subQ0=sQuery(id+"F6.wireOp",EDGE,"E21.0.10.0");var subQ1=sQuery(id+"F6.wireOp",EDGE,"E13");var subQ2=makeQuery(id+"F6.imprint","INTERSECT",VERTEX,{"disambiguationData":[OD(0.0)],"derivedFrom":[subQ1,subQ0]});Q49=makeQuery(id+"F6.imprint","IMPRINT",FACE,{"disambiguationData":[TD([[makeQuery(id+"F6.imprint","IMPRINT",EDGE,{"disambiguationData":[TD([[subQ2,-1.0]])],"derivedFrom":subQ1}),-1.0]])]});}
            var Q50;
            {var subQ0=sQuery(id+"F6.wireOp",EDGE,"E21.0.11.0");var subQ1=sQuery(id+"F6.wireOp",EDGE,"E13");var subQ2=makeQuery(id+"F6.imprint","INTERSECT",VERTEX,{"disambiguationData":[OD(0.0)],"derivedFrom":[subQ1,subQ0]});Q50=makeQuery(id+"F6.imprint","IMPRINT",FACE,{"disambiguationData":[TD([[makeQuery(id+"F6.imprint","IMPRINT",EDGE,{"disambiguationData":[TD([[subQ2,-1.0]])],"derivedFrom":subQ1}),1.0]])]});}
            var Q51;
            {var subQ0=sQuery(id+"F6.wireOp",EDGE,"E21.0.11.0");var subQ1=sQuery(id+"F6.wireOp",EDGE,"E13");var subQ2=makeQuery(id+"F6.imprint","INTERSECT",VERTEX,{"disambiguationData":[OD(0.0)],"derivedFrom":[subQ1,subQ0]});Q51=makeQuery(id+"F6.imprint","IMPRINT",FACE,{"disambiguationData":[TD([[makeQuery(id+"F6.imprint","IMPRINT",EDGE,{"disambiguationData":[TD([[subQ2,-1.0]])],"derivedFrom":subQ1}),-1.0]])]});}
            var Q52;
            {var subQ0=sQuery(id+"F6.wireOp",EDGE,"E21.0.12.0");var subQ1=sQuery(id+"F6.wireOp",EDGE,"E13");var subQ2=makeQuery(id+"F6.imprint","INTERSECT",VERTEX,{"disambiguationData":[OD(0.0)],"derivedFrom":[subQ1,subQ0]});Q52=makeQuery(id+"F6.imprint","IMPRINT",FACE,{"disambiguationData":[TD([[makeQuery(id+"F6.imprint","IMPRINT",EDGE,{"disambiguationData":[TD([[subQ2,-1.0]])],"derivedFrom":subQ1}),1.0]])]});}
            var Q53;
            {var subQ0=sQuery(id+"F6.wireOp",EDGE,"E21.0.12.0");var subQ1=sQuery(id+"F6.wireOp",EDGE,"E13");var subQ2=makeQuery(id+"F6.imprint","INTERSECT",VERTEX,{"disambiguationData":[OD(0.0)],"derivedFrom":[subQ1,subQ0]});Q53=makeQuery(id+"F6.imprint","IMPRINT",FACE,{"disambiguationData":[TD([[makeQuery(id+"F6.imprint","IMPRINT",EDGE,{"disambiguationData":[TD([[subQ2,-1.0]])],"derivedFrom":subQ1}),-1.0]])]});}
            var Q54;
            {var subQ0=sQuery(id+"F6.wireOp",EDGE,"E21.0.13.0");var subQ1=sQuery(id+"F6.wireOp",EDGE,"E13");var subQ2=makeQuery(id+"F6.imprint","INTERSECT",VERTEX,{"disambiguationData":[OD(0.0)],"derivedFrom":[subQ1,subQ0]});Q54=makeQuery(id+"F6.imprint","IMPRINT",FACE,{"disambiguationData":[TD([[makeQuery(id+"F6.imprint","IMPRINT",EDGE,{"disambiguationData":[TD([[subQ2,-1.0]])],"derivedFrom":subQ1}),1.0]])]});}
            var Q55;
            {var subQ0=sQuery(id+"F6.wireOp",EDGE,"E21.0.13.0");var subQ1=sQuery(id+"F6.wireOp",EDGE,"E13");var subQ2=makeQuery(id+"F6.imprint","INTERSECT",VERTEX,{"disambiguationData":[OD(0.0)],"derivedFrom":[subQ1,subQ0]});Q55=makeQuery(id+"F6.imprint","IMPRINT",FACE,{"disambiguationData":[TD([[makeQuery(id+"F6.imprint","IMPRINT",EDGE,{"disambiguationData":[TD([[subQ2,-1.0]])],"derivedFrom":subQ1}),-1.0]])]});}
            var Q56;
            Q56=makeQuery(id+"F5.opExtrude","SWEPT_FACE",FACE,{"disambiguationData":[OSD([sQuery(id+"F4.wireOp",EDGE,"E12.MirrorCS")])]});
            extrude(context, id + "F7", {"entities" : qUnion([Q0, Q1, Q2, Q3, Q4, Q5, Q6, Q7, Q8, Q9, Q10, Q11, Q12, Q13, Q14, Q15, Q16, Q17, Q18, Q19, Q20, Q21, Q22, Q23, Q24, Q25, Q26, Q27, Q28, Q29, Q30, Q31, Q32, Q33, Q34, Q35, Q36, Q37, Q38, Q39, Q40, Q41, Q42, Q43, Q44, Q45, Q46, Q47, Q48, Q49, Q50, Q51, Q52, Q53, Q54, Q55]), "operationType" : NewBodyOperationType.REMOVE, "endBound" : BoundingType.THROUGH_ALL, "oppositeDirection" : true, "depth" : 508 * mm, "endBoundEntityFace" : qUnion([Q56]), "offsetDistance" : 25.4 * mm});
        }
        {
            var Q0;
            Q0=makeQuery(id+"F5.opExtrude","SWEPT_FACE",FACE,{"disambiguationData":[OSD([sQuery(id+"F4.wireOp",EDGE,"E12.MirrorCS")])]});
            var sketch = newSketch(context, id + "F8", { "sketchPlane" : qUnion([Q0])});
            skLineSegment(sketch, "E24", {"start": v(-635, -40.81) * mm, "end": v(0, -40.81) * mm});
            skCircle(sketch, "E25", {"center": v(-9.53, -40.81) * mm, "radius": 3.18 * mm});
            skCircle(sketch, "E26.1.0.0", {"center": v(-53.98, -40.81) * mm, "radius": 3.18 * mm});
            skCircle(sketch, "E26.2.0.0", {"center": v(-98.43, -40.81) * mm, "radius": 3.18 * mm});
            skCircle(sketch, "E26.3.0.0", {"center": v(-142.88, -40.81) * mm, "radius": 3.18 * mm});
            skCircle(sketch, "E26.4.0.0", {"center": v(-187.33, -40.81) * mm, "radius": 3.18 * mm});
            skCircle(sketch, "E26.5.0.0", {"center": v(-231.78, -40.81) * mm, "radius": 3.18 * mm});
            skCircle(sketch, "E26.6.0.0", {"center": v(-276.23, -40.81) * mm, "radius": 3.18 * mm});
            skCircle(sketch, "E26.7.0.0", {"center": v(-320.68, -40.81) * mm, "radius": 3.18 * mm});
            skLineSegment(sketch, "E26.direction1", {"start": v(-9.53, -40.81) * mm, "end": v(-53.98, -40.81) * mm, "construction": true});
            skLineSegment(sketch, "E27", {"start": v(-635, -18.59) * mm, "end": v(0, -18.59) * mm});
            skCircle(sketch, "E28", {"center": v(-9.53, -18.59) * mm, "radius": 3.18 * mm});
            skCircle(sketch, "E29.1.0.0", {"center": v(-53.98, -18.59) * mm, "radius": 3.18 * mm});
            skCircle(sketch, "E29.2.0.0", {"center": v(-98.43, -18.59) * mm, "radius": 3.18 * mm});
            skCircle(sketch, "E29.3.0.0", {"center": v(-142.88, -18.59) * mm, "radius": 3.18 * mm});
            skCircle(sketch, "E29.4.0.0", {"center": v(-187.33, -18.59) * mm, "radius": 3.18 * mm});
            skCircle(sketch, "E29.5.0.0", {"center": v(-231.78, -18.59) * mm, "radius": 3.18 * mm});
            skCircle(sketch, "E29.6.0.0", {"center": v(-276.23, -18.59) * mm, "radius": 3.18 * mm});
            skCircle(sketch, "E29.7.0.0", {"center": v(-320.68, -18.59) * mm, "radius": 3.18 * mm});
            skLineSegment(sketch, "E29.direction1", {"start": v(-9.53, -18.59) * mm, "end": v(-53.98, -18.59) * mm, "construction": true});
            skCircle(sketch, "E30.0.8.0", {"center": v(-365.13, -40.81) * mm, "radius": 3.18 * mm});
            skCircle(sketch, "E31.0.8.0", {"center": v(-365.13, -18.59) * mm, "radius": 3.18 * mm});
            skCircle(sketch, "E32.0.9.0", {"center": v(-409.58, -40.81) * mm, "radius": 3.18 * mm});
            skCircle(sketch, "E32.0.10.0", {"center": v(-454.03, -40.81) * mm, "radius": 3.18 * mm});
            skCircle(sketch, "E32.0.11.0", {"center": v(-498.48, -40.81) * mm, "radius": 3.18 * mm});
            skCircle(sketch, "E32.0.12.0", {"center": v(-542.93, -40.81) * mm, "radius": 3.18 * mm});
            skCircle(sketch, "E32.0.13.0", {"center": v(-587.38, -40.81) * mm, "radius": 3.18 * mm});
            skCircle(sketch, "E33.0.9.0", {"center": v(-409.58, -18.59) * mm, "radius": 3.18 * mm});
            skCircle(sketch, "E33.0.10.0", {"center": v(-454.03, -18.59) * mm, "radius": 3.18 * mm});
            skCircle(sketch, "E33.0.11.0", {"center": v(-498.48, -18.59) * mm, "radius": 3.18 * mm});
            skCircle(sketch, "E33.0.12.0", {"center": v(-542.93, -18.59) * mm, "radius": 3.18 * mm});
            skCircle(sketch, "E33.0.13.0", {"center": v(-587.38, -18.59) * mm, "radius": 3.18 * mm});
            skSolve(sketch);
        }
        {
            var Q0;
            Q0 = qSketchRegion(id + "F8", true);
            extrude(context, id + "F9", {"entities" : qUnion([Q0]), "operationType" : NewBodyOperationType.REMOVE, "endBound" : BoundingType.THROUGH_ALL, "oppositeDirection" : true, "depth" : 25.4 * mm, "offsetDistance" : 25.4 * mm});
        }
        {
            var Q0;
            Q0=makeQuery(id+"F5.opExtrude","SWEPT_FACE",FACE,{"disambiguationData":[OSD([sQuery(id+"F4.wireOp",EDGE,"E3.bottom")])]});
            var sketch = newSketch(context, id + "F10", { "sketchPlane" : qUnion([Q0])});
            skLineSegment(sketch, "E34.bottom", {"start": v(0, 284.48) * mm, "end": v(38.1, 284.48) * mm});
            skLineSegment(sketch, "E34.top", {"start": v(0, 246.38) * mm, "end": v(38.1, 246.38) * mm});
            skLineSegment(sketch, "E34.left", {"start": v(0, 284.48) * mm, "end": v(0, 246.38) * mm});
            skLineSegment(sketch, "E34.right", {"start": v(38.1, 284.48) * mm, "end": v(38.1, 246.38) * mm});
            skLineSegment(sketch, "E35.bottom", {"start": v(0, -284.78) * mm, "end": v(38.1, -284.78) * mm});
            skLineSegment(sketch, "E35.top", {"start": v(0, -246.68) * mm, "end": v(38.1, -246.68) * mm});
            skLineSegment(sketch, "E35.left", {"start": v(0, -284.78) * mm, "end": v(0, -246.68) * mm});
            skLineSegment(sketch, "E35.right", {"start": v(38.1, -284.78) * mm, "end": v(38.1, -246.68) * mm});
            skLineSegment(sketch, "E36.bottom", {"start": v(635, -284.78) * mm, "end": v(596.9, -284.78) * mm});
            skLineSegment(sketch, "E36.top", {"start": v(635, -246.68) * mm, "end": v(596.9, -246.68) * mm});
            skLineSegment(sketch, "E36.left", {"start": v(635, -284.78) * mm, "end": v(635, -246.68) * mm});
            skLineSegment(sketch, "E36.right", {"start": v(596.9, -284.78) * mm, "end": v(596.9, -246.68) * mm});
            skLineSegment(sketch, "E37.bottom", {"start": v(635, 246.38) * mm, "end": v(596.9, 246.38) * mm});
            skLineSegment(sketch, "E37.top", {"start": v(635, 284.48) * mm, "end": v(596.9, 284.48) * mm});
            skLineSegment(sketch, "E37.left", {"start": v(635, 246.38) * mm, "end": v(635, 284.48) * mm});
            skLineSegment(sketch, "E37.right", {"start": v(596.9, 246.38) * mm, "end": v(596.9, 284.48) * mm});
            skSolve(sketch);
        }
        {
            var Q0;
            Q0 = qSketchRegion(id + "F10", true);
            extrude(context, id + "F11", {"entities" : qUnion([Q0]), "operationType" : NewBodyOperationType.ADD, "depth" : 247.82 * mm, "offsetDistance" : 25.4 * mm});
        }
    });
